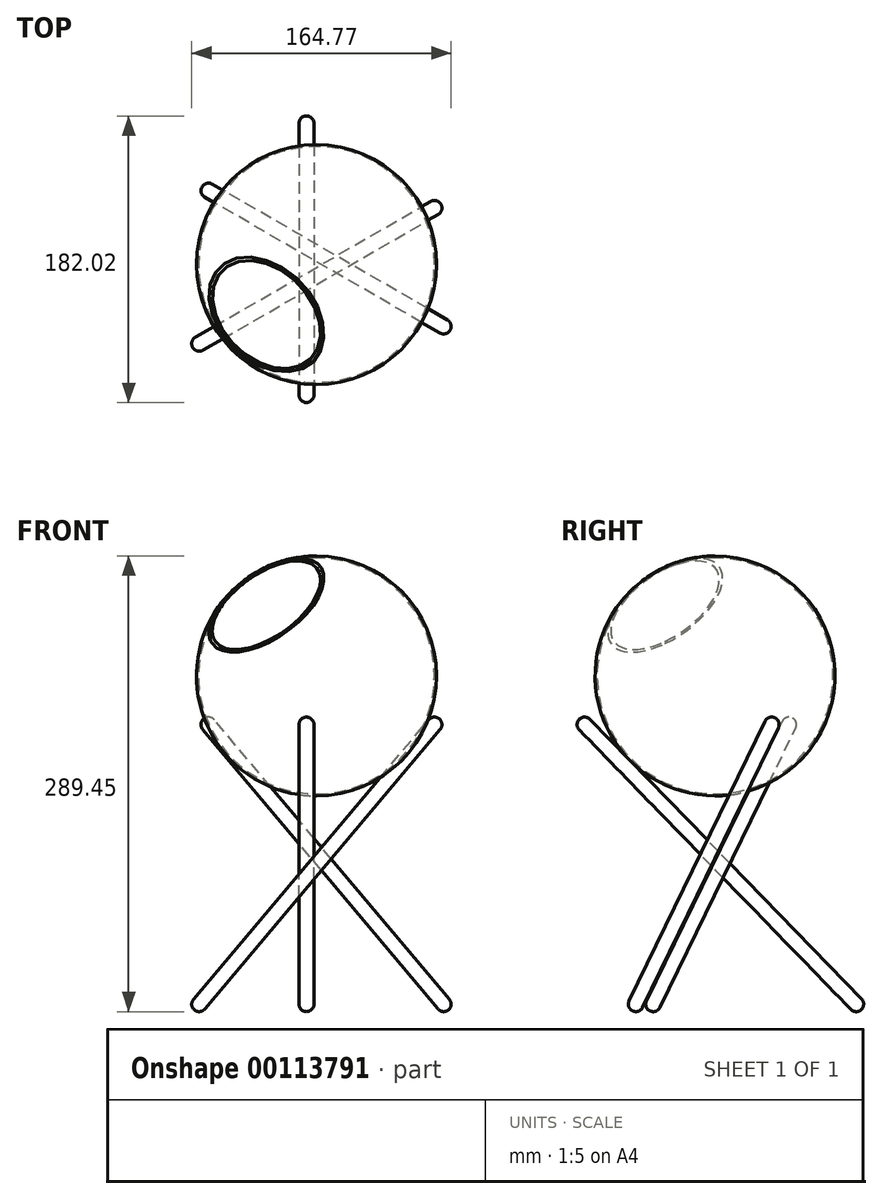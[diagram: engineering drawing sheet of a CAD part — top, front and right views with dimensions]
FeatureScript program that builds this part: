
annotation { "Feature Type Name" : "Feature", "Feature Type Description" : "" }
export const myFeature = defineFeature(function(context is Context, id is Id, definition is map)
    precondition{}
    {
        {
            var Q0;
            Q0=qCreatedBy(makeId("Front.planeOp"),FACE);
            var sketch = newSketch(context, id + "F0", { "sketchPlane" : qUnion([Q0])});
            skArc(sketch, "E0", {"start": v(0, -76.2) * mm, "mid": v(76.2, 0) * mm, "end": v(0, 76.2) * mm});
            skLineSegment(sketch, "E1", {"start": v(0, 76.2) * mm, "end": v(0, -76.2) * mm});
            skSolve(sketch);
        }
        {
            var Q0;
            Q0 = qSketchRegion(id + "F0", true);
            var Q1;
            Q1=sQuery(id+"F0.wireOp",EDGE,"E1");
            revolve(context, id + "F1", {"entities" : qUnion([Q0]), "axis" : qUnion([Q1]), "revolveType" : RevolveType.FULL});
        }
        {
            var Q0;
            Q0=qCreatedBy(makeId("Top.planeOp"),FACE);
            cPlane(context, id + "F2", {"entities" : qUnion([Q0]), "cplaneType" : CPlaneType.OFFSET, "offset" : 69.85 * mm, "oppositeDirection" : true, "width" : 152.4 * mm, "height" : 152.4 * mm});
        }
        {
            var Q0;
            Q0=qCreatedBy(makeId("Right.planeOp"),FACE);
            var Q1;
            Q1=qCreatedBy(makeId("Front.planeOp"),FACE);
            cPlane(context, id + "F3", {"entities" : qUnion([Q0, Q1]), "cplaneType" : CPlaneType.MID_PLANE, "offset" : 25.4 * mm, "width" : 152.4 * mm, "height" : 152.4 * mm});
        }
        {
            var Q0;
            Q0=qCreatedBy(id+"F3.planeOp",FACE);
            var Q1;
            Q1=qCreatedBy(makeId("Top.planeOp"),FACE);
            cPlane(context, id + "F4", {"entities" : qUnion([Q0, Q1]), "cplaneType" : CPlaneType.MID_PLANE, "offset" : 25.4 * mm, "width" : 152.4 * mm, "height" : 152.4 * mm});
        }
        {
            var Q0;
            Q0=qCreatedBy(id+"F4.planeOp",FACE);
            cPlane(context, id + "F5", {"entities" : qUnion([Q0]), "cplaneType" : CPlaneType.OFFSET, "offset" : 63.5 * mm, "oppositeDirection" : true, "width" : 152.4 * mm, "height" : 152.4 * mm});
        }
        {
            var Q0;
            Q0=qCreatedBy(id+"F5.planeOp",FACE);
            var sketch = newSketch(context, id + "F6", { "sketchPlane" : qUnion([Q0])});
            skCircle(sketch, "E2", {"center": v(0, 0) * mm, "radius": 81.65 * mm});
            skSolve(sketch);
        }
        {
            var Q0;
            Q0=makeQuery(id+"F6.imprint","IMPRINT",FACE,{"disambiguationData":[TD([[makeQuery(id+"F6.imprint","IMPRINT",EDGE,{"derivedFrom":sQuery(id+"F6.wireOp",EDGE,"E2")}),1.0]])]});
            extrude(context, id + "F7", {"entities" : qUnion([Q0]), "operationType" : NewBodyOperationType.REMOVE, "oppositeDirection" : true, "depth" : 12.7 * mm});
        }
        {
            var Q0;
            Q0=makeQuery(id+"F7.boolean.opBoolean","COPY",FACE,{"derivedFrom":makeQuery(id+"F7.opExtrude","CAP_FACE",FACE,{"disambiguationData":[OSD([sQuery(id+"F6.wireOp",EDGE,"E2")])],"isStart":true})});
            shell(context, id + "F8", {"entities" : qUnion([Q0]), "thickness" : 1.27 * mm});
        }
        {
            var Q0;
            Q0=qCreatedBy(makeId("Right.planeOp"),FACE);
            var sketch = newSketch(context, id + "F9", { "sketchPlane" : qUnion([Q0])});
            skArc(sketch, "E3", {"start": v(30.45, -69.85) * mm, "mid": v(0, 76.2) * mm, "end": v(-30.45, -69.85) * mm});
            skLineSegment(sketch, "E4", {"start": v(-79.45, -27.57) * mm, "end": v(93.05, -205.17) * mm});
            skPoint(sketch, "E5", {"position": v(-79.45, -27.57) * mm});
            skLineSegment(sketch, "E6.0", {"start": v(-81.73, -29.78) * mm, "end": v(90.77, -207.38) * mm});
            skLineSegment(sketch, "E7", {"start": v(-81.73, -29.78) * mm, "end": v(-79.45, -27.57) * mm});
            skLineSegment(sketch, "E8", {"start": v(90.77, -207.38) * mm, "end": v(93.05, -205.17) * mm});
            skSolve(sketch);
        }
        {
            var Q0;
            Q0=qCreatedBy(makeId("Right.planeOp"),FACE);
            cPlane(context, id + "F10", {"entities" : qUnion([Q0]), "cplaneType" : CPlaneType.OFFSET, "offset" : 6.35 * mm, "oppositeDirection" : true, "width" : 152.4 * mm, "height" : 152.4 * mm});
        }
        {
            var Q0;
            Q0=qCreatedBy(id+"F10.planeOp",FACE);
            var sketch = newSketch(context, id + "F11", { "sketchPlane" : qUnion([Q0])});
            skLineSegment(sketch, "E9.0", {"start": v(-79.45, -27.57) * mm, "end": v(93.05, -205.17) * mm});
            skLineSegment(sketch, "E10.0", {"start": v(-86.18, -27.47) * mm, "end": v(92.95, -211.9) * mm});
            skPoint(sketch, "E11.orphan", {"position": v(-81.73, -29.78) * mm});
            skPoint(sketch, "E12.orphan", {"position": v(90.77, -207.38) * mm});
            skArc(sketch, "E13", {"start": v(-79.45, -27.57) * mm, "mid": v(-82.8, -26.13) * mm, "end": v(-86.18, -27.47) * mm});
            skPoint(sketch, "E14.0.end.orphan", {"position": v(-79.45, -27.57) * mm});
            skArc(sketch, "E15", {"start": v(92.95, -211.9) * mm, "mid": v(94.4, -208.55) * mm, "end": v(93.05, -205.17) * mm});
            skPoint(sketch, "E16.0.end.orphan", {"position": v(93.05, -205.17) * mm});
            skSolve(sketch);
        }
        {
            var Q0;
            Q0=makeQuery(id+"F11.imprint","IMPRINT",FACE,{"disambiguationData":[TD([[makeQuery(id+"F11.imprint","IMPRINT",EDGE,{"derivedFrom":sQuery(id+"F11.wireOp",EDGE,"E9.0")}),-1.0]])]});
            var Q1;
            Q1=sQuery(id+"F11.wireOp",EDGE,"E10.0");
            revolve(context, id + "F12", {"entities" : qUnion([Q0]), "axis" : qUnion([Q1]), "revolveType" : RevolveType.FULL});
        }
        {
            var Q0;
            Q0=qCreatedBy(makeId("Right.planeOp"),FACE);
            var sketch = newSketch(context, id + "F13", { "sketchPlane" : qUnion([Q0])});
            skLineSegment(sketch, "E17", {"start": v(0, 77.82) * mm, "end": v(0, -75.9) * mm});
            skLineSegment(sketch, "E18.0", {"start": v(-6.35, 77.82) * mm, "end": v(-6.35, -75.9) * mm});
            skSolve(sketch);
        }
        {
            var Q0;
            Q0=makeQuery(id+"F12.opRevolve","SWEPT_BODY",BODY,{"disambiguationData":[OSD([sQuery(id+"F11.wireOp",EDGE,"a594fcbd-cb68-4209-80de-baa63116bc36.0"),sQuery(id+"F11.wireOp",EDGE,"E9.0"),sQuery(id+"F11.wireOp",EDGE,"E14.0"),sQuery(id+"F11.wireOp",EDGE,"E16.0")])]});
            var Q1;
            Q1=sQuery(id+"F13.wireOp",EDGE,"E17");
            circularPattern(context, id + "F14", {"entities" : qUnion([Q0]), "axis" : qUnion([Q1]), "angle" : 360 * degree, "instanceCount" : 3, "equalSpace" : true});
        }
    });
